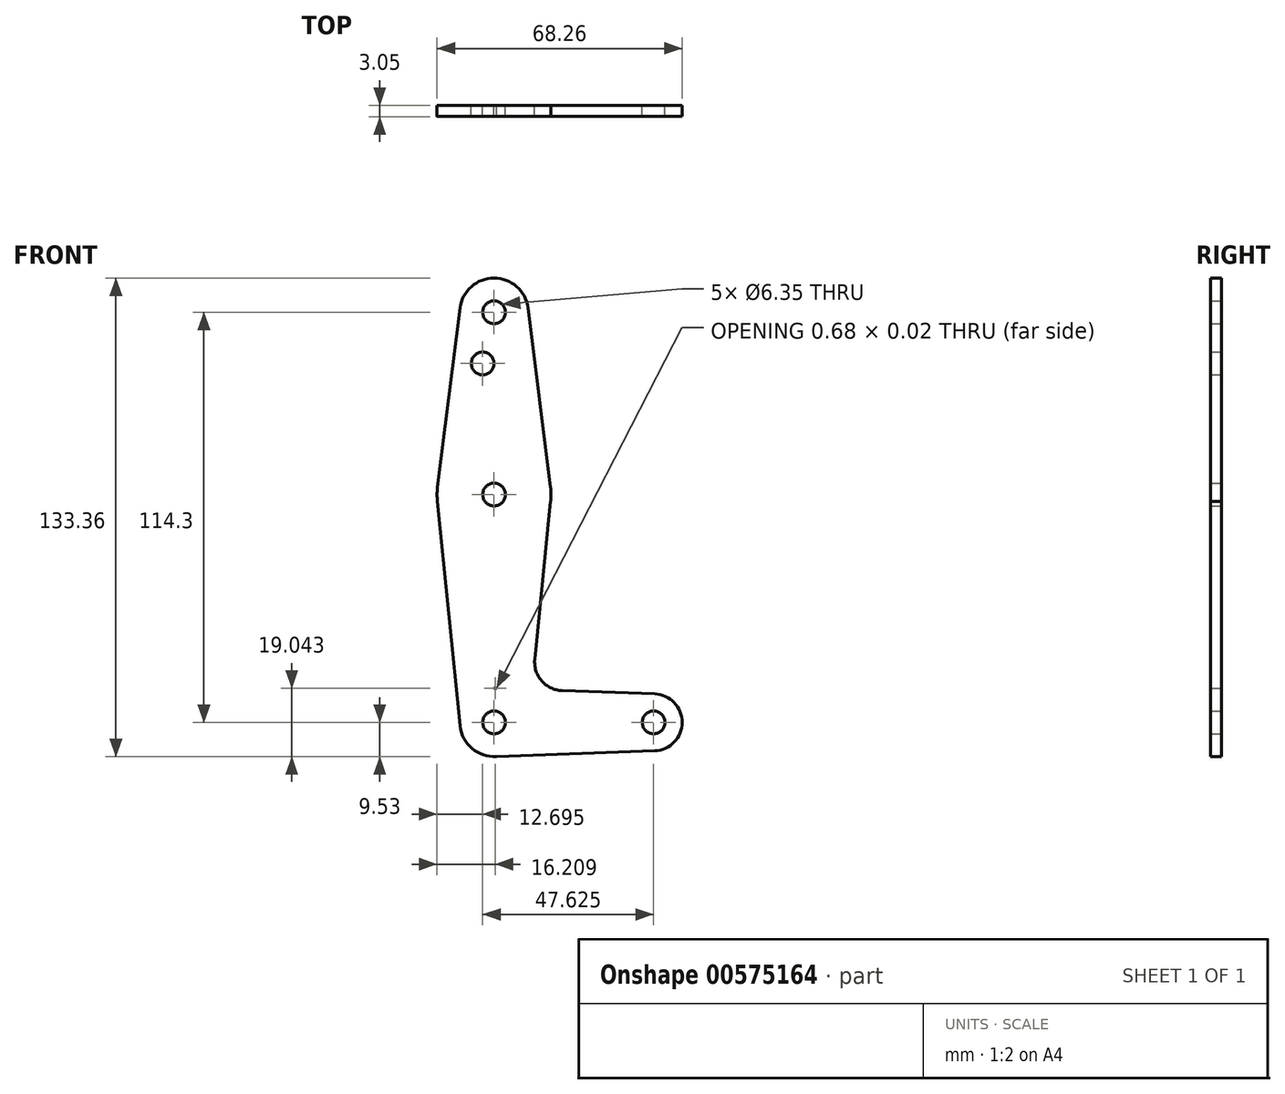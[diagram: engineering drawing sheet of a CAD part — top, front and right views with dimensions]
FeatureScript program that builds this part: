
annotation { "Feature Type Name" : "Feature", "Feature Type Description" : "" }
export const myFeature = defineFeature(function(context is Context, id is Id, definition is map)
    precondition{}
    {
        {
            var Q0;
            Q0=qCreatedBy(makeId("Front.planeOp"),FACE);
            var sketch = newSketch(context, id + "F0", { "sketchPlane" : qUnion([Q0])});
            skLineSegment(sketch, "E0", {"start": v(0, 0) * mm, "end": v(0, 114.3) * mm, "construction": true});
            skLineSegment(sketch, "E1", {"start": v(0, 0) * mm, "end": v(44.45, 0) * mm, "construction": true});
            skCircle(sketch, "E2", {"center": v(0, 63.5) * mm, "radius": 15.88 * mm});
            skCircle(sketch, "E3", {"center": v(0, 114.3) * mm, "radius": 9.53 * mm});
            skCircle(sketch, "E4", {"center": v(0, 0) * mm, "radius": 9.53 * mm});
            skCircle(sketch, "E5", {"center": v(44.45, 0) * mm, "radius": 7.94 * mm});
            skLineSegment(sketch, "E6", {"start": v(-9.45, 115.5) * mm, "end": v(-15.75, 65.48) * mm});
            skLineSegment(sketch, "E7", {"start": v(9.45, 115.5) * mm, "end": v(15.75, 65.48) * mm});
            skLineSegment(sketch, "E8", {"start": v(0, -9.53) * mm, "end": v(44.73, -7.93) * mm});
            skCircle(sketch, "E9", {"center": v(-3.18, 100.03) * mm, "radius": 3.18 * mm});
            skCircle(sketch, "E10", {"center": v(0, 0) * mm, "radius": 3.18 * mm});
            skCircle(sketch, "E11", {"center": v(44.45, 0) * mm, "radius": 3.18 * mm});
            skCircle(sketch, "E12", {"center": v(0, 63.5) * mm, "radius": 3.18 * mm});
            skCircle(sketch, "E13", {"center": v(0, 114.3) * mm, "radius": 3.18 * mm});
            skPoint(sketch, "E14.newPointB", {"position": v(0, 9.53) * mm});
            skLineSegment(sketch, "E15", {"start": v(-15.75, 61.52) * mm, "end": v(-9.48, -0.95) * mm});
            skLineSegment(sketch, "E16", {"start": v(15.75, 61.52) * mm, "end": v(11.34, 17.59) * mm});
            skLineSegment(sketch, "E17", {"start": v(44.73, 7.93) * mm, "end": v(18.97, 8.85) * mm});
            skLineSegment(sketch, "E18.trimOffspring", {"start": v(0.68, 9.5) * mm, "end": v(0, 9.53) * mm});
            skLineSegment(sketch, "E19.trimOffspring", {"start": v(9.57, 0) * mm, "end": v(9.48, -0.95) * mm});
            skPoint(sketch, "E20.visualSharp", {"position": v(10.5, 9.15) * mm});
            skArc(sketch, "E20.filletArc", {"start": v(11.34, 17.59) * mm, "mid": v(13.26, 11.57) * mm, "end": v(18.97, 8.85) * mm});
            skSolve(sketch);
        }
        {
            var Q0;
            Q0 = qSketchRegion(id + "F0", true);
            extrude(context, id + "F1", {"entities" : qUnion([Q0]), "depth" : 3.05 * mm, "offsetDistance" : 25.4 * mm});
        }
    });
